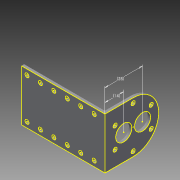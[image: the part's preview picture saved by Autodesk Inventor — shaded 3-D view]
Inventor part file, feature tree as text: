
AUTODESK INVENTOR PART (.ipt)
format: ipt  version: 2013 (Build 170138000, 138)  size: 174,080 bytes
history: native  units: mm
features: sketch x6, extrude x3, other x1, hole x1, fillet x1
ambient origin geometry x8: Origin, YZ Plane, XZ Plane, XY Plane, X Axis, Y Axis, Z Axis, Center Point
feature tree (12):
  other  "ソリッド1"
  extrude  "押し出し1"  Depth=62.0mm
  hole  "穴1"  [1 undecoded]
  extrude  "押し出し2"  Depth=2.0mm TaperAngle=0.0deg
  fillet  "フィレット1"  Radius=4.0mm
  extrude  "押し出し3"  Depth=4.0mm
  sketch  "スケッチ5"
  sketch  "スケッチ6"
  sketch  "スケッチ1"
  sketch  "スケッチ2"
  sketch  "スケッチ3"
  sketch  "スケッチ4"
note: 1 required parameter value undecoded (feature->parameter linkage not recoverable at this tier; creation-order binding heuristic only, values carry confidence <= 0.55)
